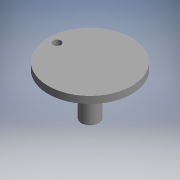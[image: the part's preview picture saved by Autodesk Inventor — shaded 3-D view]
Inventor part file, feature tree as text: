
AUTODESK INVENTOR PART (.ipt)
format: ipt  version: 2017 (Build 210142000, 142)  size: 85,504 bytes
history: native  units: mm (DEFAULTED — no unit token found)
features: extrude x3, sketch x3
ambient origin geometry x8: Origin, YZ Plane, XZ Plane, XY Plane, X Axis, Y Axis, Z Axis, Center Point
bodies: Solid1 (feature_tree)
feature tree (6):
  extrude  "Extrusion1"  Depth=5.0mm
  extrude  "Extrusion2"  Depth=12.0mm
  extrude  "Extrusion3"  Depth=10.0mm TaperAngle=0.0deg
  sketch  "Sketch1"  dims[d3=0.0mm d4=5.0mm]
  sketch  "Sketch2"  dims[d5=12.0mm d6=0.0mm d8=9.481236mm]
  sketch  "Sketch3"  dims[d9=2.253101mm d10=10.0mm d11=0.0mm]
